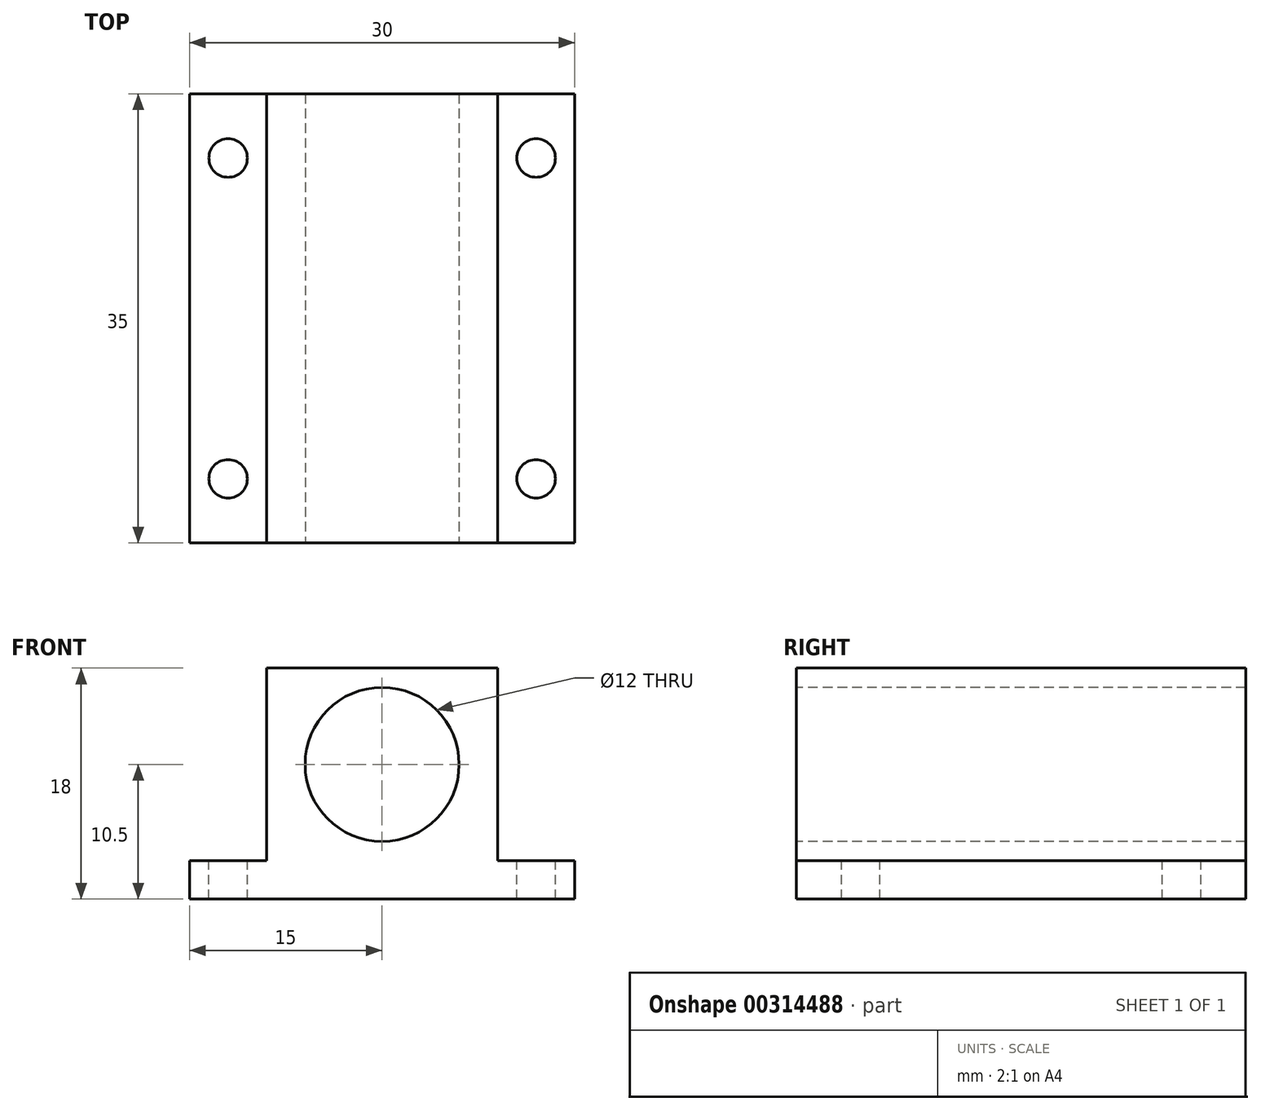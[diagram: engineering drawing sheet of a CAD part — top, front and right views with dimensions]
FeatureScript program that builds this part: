
annotation { "Feature Type Name" : "Feature", "Feature Type Description" : "" }
export const myFeature = defineFeature(function(context is Context, id is Id, definition is map)
    precondition{}
    {
        {
            var Q0;
            Q0=qCreatedBy(makeId("Top.planeOp"),FACE);
            var sketch = newSketch(context, id + "F0", { "sketchPlane" : qUnion([Q0])});
            skLineSegment(sketch, "E0.bottom", {"start": v(-15, -17.5) * mm, "end": v(15, -17.5) * mm});
            skLineSegment(sketch, "E0.top", {"start": v(-15, 17.5) * mm, "end": v(15, 17.5) * mm});
            skLineSegment(sketch, "E0.left", {"start": v(-15, -17.5) * mm, "end": v(-15, 17.5) * mm});
            skLineSegment(sketch, "E0.right", {"start": v(15, -17.5) * mm, "end": v(15, 17.5) * mm});
            skPoint(sketch, "E0.middle", {"position": v(0, 0) * mm});
            skSolve(sketch);
        }
        {
            var Q0;
            Q0=makeQuery(id+"F0.imprint","IMPRINT",FACE,{"disambiguationData":[TD([[makeQuery(id+"F0.imprint","IMPRINT",EDGE,{"derivedFrom":sQuery(id+"F0.wireOp",EDGE,"E0.bottom")}),1.0]])]});
            extrude(context, id + "F1", {"entities" : qUnion([Q0]), "depth" : 3 * mm});
        }
        {
            var Q0;
            Q0=makeQuery(id+"F1.opExtrude","SWEPT_FACE",FACE,{"disambiguationData":[OSD([sQuery(id+"F0.wireOp",EDGE,"E0.bottom")])]});
            var sketch = newSketch(context, id + "F2", { "sketchPlane" : qUnion([Q0])});
            skLineSegment(sketch, "E1", {"start": v(0, 0) * mm, "end": v(-9, 0) * mm});
            skLineSegment(sketch, "E2", {"start": v(-9, 0) * mm, "end": v(-9, 18) * mm});
            skLineSegment(sketch, "E3", {"start": v(-9, 18) * mm, "end": v(9, 18) * mm});
            skLineSegment(sketch, "E4", {"start": v(9, 18) * mm, "end": v(9, 0) * mm});
            skLineSegment(sketch, "E5", {"start": v(9, 0) * mm, "end": v(0, 0) * mm});
            skSolve(sketch);
        }
        {
            var Q0;
            {var subQ0=sQuery(id+"F2.wireOp",EDGE,"E3");Q0=makeQuery(id+"F2.imprint","IMPRINT",FACE,{"disambiguationData":[TD([[makeQuery(id+"F2.imprint","IMPRINT",EDGE,{"derivedFrom":subQ0}),-1.0]])]});}
            extrude(context, id + "F3", {"entities" : qUnion([Q0]), "operationType" : NewBodyOperationType.ADD, "oppositeDirection" : true, "depth" : 35 * mm});
        }
        {
            var Q0;
            {var subQ0=sQuery(id+"F0.wireOp",EDGE,"E0.bottom");Q0=makeQuery(id+"F3.boolean.opBoolean","MERGE",FACE,{"derivedFrom":[makeQuery(id+"F1.opExtrude","SWEPT_FACE",FACE,{"disambiguationData":[OSD([subQ0])]}),makeQuery(id+"F3.opExtrude","CAP_FACE",FACE,{"disambiguationData":[OSD([subQ0,sQuery(id+"F2.wireOp",EDGE,"E2"),sQuery(id+"F2.wireOp",EDGE,"E3"),sQuery(id+"F2.wireOp",EDGE,"E4")])],"isStart":true})]});}
            var sketch = newSketch(context, id + "F4", { "sketchPlane" : qUnion([Q0])});
            skCircle(sketch, "E6", {"center": v(0, 10.5) * mm, "radius": 6 * mm});
            skPoint(sketch, "E6.centerSnap0", {"position": v(9, 10.5) * mm});
            skPoint(sketch, "E6.centerSnap1", {"position": v(0, 18) * mm});
            skSolve(sketch);
        }
        {
            var Q0;
            Q0=makeQuery(id+"F4.imprint","IMPRINT",FACE,{"disambiguationData":[TD([[makeQuery(id+"F4.imprint","IMPRINT",EDGE,{"derivedFrom":sQuery(id+"F4.wireOp",EDGE,"E6")}),1.0]])]});
            extrude(context, id + "F5", {"entities" : qUnion([Q0]), "operationType" : NewBodyOperationType.REMOVE, "oppositeDirection" : true, "depth" : 40 * mm});
        }
        {
            var Q0;
            {var subQ3=sQuery(id+"F0.wireOp",EDGE,"E0.bottom");var subQ4=sQuery(id+"F0.wireOp",EDGE,"E0.top");var subQ5=sQuery(id+"F0.wireOp",EDGE,"E0.right");Q0=makeQuery(id+"F3.boolean.opBoolean","SPLIT",FACE,{"disambiguationData":[TD([makeQuery(id+"F1.opExtrude","SWEPT_FACE",FACE,{"disambiguationData":[OSD([subQ5])]})])],"derivedFrom":makeQuery(id+"F1.opExtrude","CAP_FACE",FACE,{"disambiguationData":[OSD([subQ3,subQ4,sQuery(id+"F0.wireOp",EDGE,"E0.left"),subQ5])],"isStart":false})});}
            var sketch = newSketch(context, id + "F6", { "sketchPlane" : qUnion([Q0])});
            skLineSegment(sketch, "E7", {"start": v(12, 17.5) * mm, "end": v(12, -17.5) * mm, "construction": true});
            skCircle(sketch, "E8", {"center": v(12, 12.5) * mm, "radius": 1.5 * mm});
            skCircle(sketch, "E9", {"center": v(12, -12.5) * mm, "radius": 1.5 * mm});
            skCircle(sketch, "E10.MirrorC", {"center": v(-12, -12.5) * mm, "radius": 1.5 * mm});
            skCircle(sketch, "E11.MirrorC", {"center": v(-12, 12.5) * mm, "radius": 1.5 * mm});
            skSolve(sketch);
        }
        {
            var Q0;
            Q0 = qSketchRegion(id + "F6", true);
            extrude(context, id + "F7", {"entities" : qUnion([Q0]), "operationType" : NewBodyOperationType.REMOVE, "oppositeDirection" : true, "depth" : 25 * mm});
        }
    });
